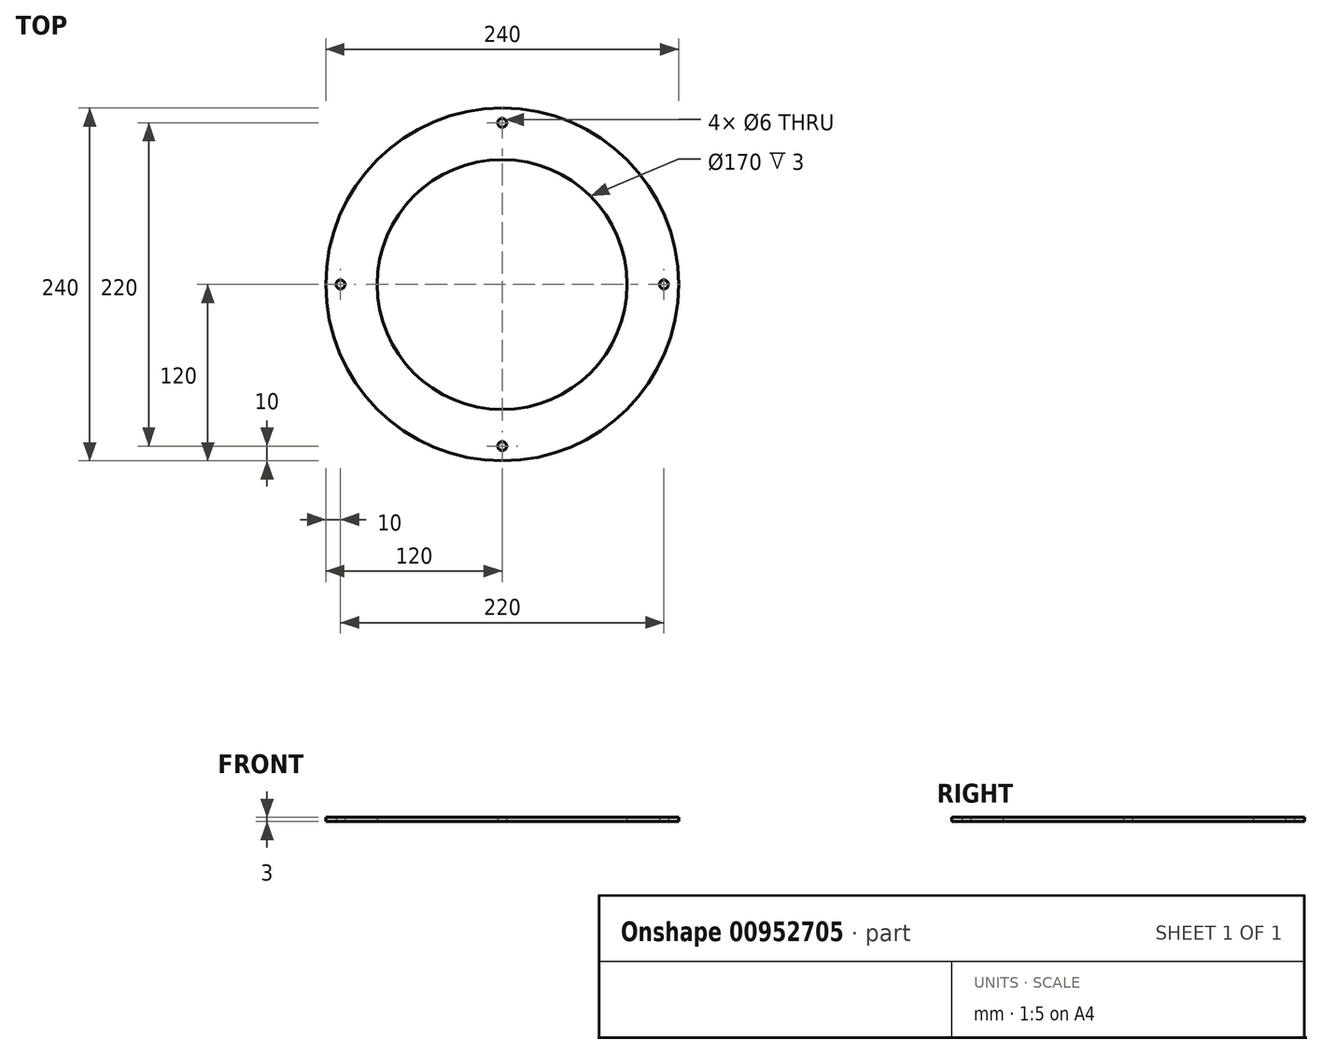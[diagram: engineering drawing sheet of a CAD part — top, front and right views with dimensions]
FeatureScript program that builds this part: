
annotation { "Feature Type Name" : "Feature", "Feature Type Description" : "" }
export const myFeature = defineFeature(function(context is Context, id is Id, definition is map)
    precondition{}
    {
        {
            var Q0;
            Q0=qCreatedBy(makeId("Top.planeOp"),FACE);
            var sketch = newSketch(context, id + "F0", { "sketchPlane" : qUnion([Q0])});
            skCircle(sketch, "E0", {"center": v(0, 0) * mm, "radius": 120 * mm});
            skCircle(sketch, "E1", {"center": v(0, 0) * mm, "radius": 85 * mm});
            skCircle(sketch, "E2", {"center": v(-110, 0) * mm, "radius": 3 * mm});
            skCircle(sketch, "E3.1.0", {"center": v(0, -110) * mm, "radius": 3 * mm});
            skCircle(sketch, "E3.2.0", {"center": v(110, 0) * mm, "radius": 3 * mm});
            skCircle(sketch, "E3.3.0", {"center": v(0, 110) * mm, "radius": 3 * mm});
            skSolve(sketch);
        }
        {
            var Q0;
            Q0 = qSketchRegion(id + "F0", true);
            var Q1;
            Q1=makeQuery(id+"F0.imprint","IMPRINT",FACE,{"disambiguationData":[TD([[makeQuery(id+"F0.imprint","IMPRINT",EDGE,{"derivedFrom":sQuery(id+"F0.wireOp",EDGE,"QZiQpIBd-OX1G-OAif-aXQa-GEJj8OLQS2Fv")}),1.0]])]});
            var Q2;
            Q2=makeQuery(id+"F0.imprint","IMPRINT",FACE,{"disambiguationData":[TD([[makeQuery(id+"F0.imprint","IMPRINT",EDGE,{"derivedFrom":sQuery(id+"F0.wireOp",EDGE,"QZiQpIBd-OX1G-OAif-aXQa-GEJj8OLQS2Fv")}),-1.0]])]});
            var Q3;
            {var subQ0=sQuery(id+"F0.wireOp",EDGE,"5mkoiHJi-mEIj-fVSE-QABf-XuZV9RVfXAw1");var subQ1=sQuery(id+"F0.wireOp",EDGE,"DTBaatzW-mmmO-AkyP-79DW-lQNtZL5bEDpv");var subQ2=makeQuery(id+"F0.imprint","INTERSECT",VERTEX,{"disambiguationData":[OD(1.0)],"derivedFrom":[subQ1,subQ0]});Q3=makeQuery(id+"F0.imprint","IMPRINT",FACE,{"disambiguationData":[TD([[makeQuery(id+"F0.imprint","IMPRINT",EDGE,{"disambiguationData":[TD([[subQ2,-1.0]])],"derivedFrom":subQ1}),1.0]])]});}
            var Q4;
            {var subQ0=sQuery(id+"F0.wireOp",EDGE,"5mkoiHJi-mEIj-fVSE-QABf-XuZV9RVfXAw1");var subQ1=sQuery(id+"F0.wireOp",EDGE,"DTBaatzW-mmmO-AkyP-79DW-lQNtZL5bEDpv");var subQ2=makeQuery(id+"F0.imprint","INTERSECT",VERTEX,{"disambiguationData":[OD(1.0)],"derivedFrom":[subQ1,subQ0]});Q4=makeQuery(id+"F0.imprint","IMPRINT",FACE,{"disambiguationData":[TD([[makeQuery(id+"F0.imprint","IMPRINT",EDGE,{"disambiguationData":[TD([[subQ2,-1.0]])],"derivedFrom":subQ1}),-1.0]])]});}
            var Q5;
            {var subQ0=sQuery(id+"F0.wireOp",EDGE,"E2");var subQ1=sQuery(id+"F0.wireOp",EDGE,"DTBaatzW-mmmO-AkyP-79DW-lQNtZL5bEDpv");var subQ2=makeQuery(id+"F0.imprint","INTERSECT",VERTEX,{"disambiguationData":[OD(1.0)],"derivedFrom":[subQ1,subQ0]});Q5=makeQuery(id+"F0.imprint","IMPRINT",FACE,{"disambiguationData":[TD([[makeQuery(id+"F0.imprint","IMPRINT",EDGE,{"disambiguationData":[TD([[subQ2,-1.0]])],"derivedFrom":subQ1}),1.0]])]});}
            var Q6;
            {var subQ0=sQuery(id+"F0.wireOp",EDGE,"E2");var subQ1=sQuery(id+"F0.wireOp",EDGE,"DTBaatzW-mmmO-AkyP-79DW-lQNtZL5bEDpv");var subQ2=makeQuery(id+"F0.imprint","INTERSECT",VERTEX,{"disambiguationData":[OD(1.0)],"derivedFrom":[subQ1,subQ0]});Q6=makeQuery(id+"F0.imprint","IMPRINT",FACE,{"disambiguationData":[TD([[makeQuery(id+"F0.imprint","IMPRINT",EDGE,{"disambiguationData":[TD([[subQ2,-1.0]])],"derivedFrom":subQ1}),-1.0]])]});}
            var Q7;
            {var subQ0=sQuery(id+"F0.wireOp",EDGE,"FiI9Vmjg-XlOb-GEvl-WWXd-EyHFkMBmwKV2");var subQ1=sQuery(id+"F0.wireOp",EDGE,"DTBaatzW-mmmO-AkyP-79DW-lQNtZL5bEDpv");var subQ2=makeQuery(id+"F0.imprint","INTERSECT",VERTEX,{"disambiguationData":[OD(1.0)],"derivedFrom":[subQ1,subQ0]});Q7=makeQuery(id+"F0.imprint","IMPRINT",FACE,{"disambiguationData":[TD([[makeQuery(id+"F0.imprint","IMPRINT",EDGE,{"disambiguationData":[TD([[subQ2,-1.0]])],"derivedFrom":subQ1}),-1.0]])]});}
            var Q8;
            {var subQ0=sQuery(id+"F0.wireOp",EDGE,"FiI9Vmjg-XlOb-GEvl-WWXd-EyHFkMBmwKV2");var subQ1=sQuery(id+"F0.wireOp",EDGE,"DTBaatzW-mmmO-AkyP-79DW-lQNtZL5bEDpv");var subQ2=makeQuery(id+"F0.imprint","INTERSECT",VERTEX,{"disambiguationData":[OD(1.0)],"derivedFrom":[subQ1,subQ0]});Q8=makeQuery(id+"F0.imprint","IMPRINT",FACE,{"disambiguationData":[TD([[makeQuery(id+"F0.imprint","IMPRINT",EDGE,{"disambiguationData":[TD([[subQ2,-1.0]])],"derivedFrom":subQ1}),1.0]])]});}
            var Q9;
            {var subQ0=sQuery(id+"F0.wireOp",EDGE,"5mkoiHJi-mEIj-fVSE-QABf-XuZV9RVfXAw1");var subQ1=sQuery(id+"F0.wireOp",EDGE,"DTBaatzW-mmmO-AkyP-79DW-lQNtZL5bEDpv");var subQ2=makeQuery(id+"F0.imprint","INTERSECT",VERTEX,{"disambiguationData":[OD(0.0)],"derivedFrom":[subQ1,subQ0]});Q9=makeQuery(id+"F0.imprint","IMPRINT",FACE,{"disambiguationData":[TD([[makeQuery(id+"F0.imprint","IMPRINT",EDGE,{"disambiguationData":[TD([[subQ2,1.0]])],"derivedFrom":subQ1}),1.0]])]});}
            var Q10;
            {var subQ0=sQuery(id+"F0.wireOp",EDGE,"5mkoiHJi-mEIj-fVSE-QABf-XuZV9RVfXAw1");var subQ1=sQuery(id+"F0.wireOp",EDGE,"DTBaatzW-mmmO-AkyP-79DW-lQNtZL5bEDpv");var subQ2=makeQuery(id+"F0.imprint","INTERSECT",VERTEX,{"disambiguationData":[OD(0.0)],"derivedFrom":[subQ1,subQ0]});Q10=makeQuery(id+"F0.imprint","IMPRINT",FACE,{"disambiguationData":[TD([[makeQuery(id+"F0.imprint","IMPRINT",EDGE,{"disambiguationData":[TD([[subQ2,1.0]])],"derivedFrom":subQ1}),-1.0]])]});}
            extrude(context, id + "F1", {"entities" : qUnion([Q0, Q1, Q2, Q3, Q4, Q5, Q6, Q7, Q8, Q9, Q10]), "depth" : 3 * mm, "offsetDistance" : 25 * mm});
        }
    });
